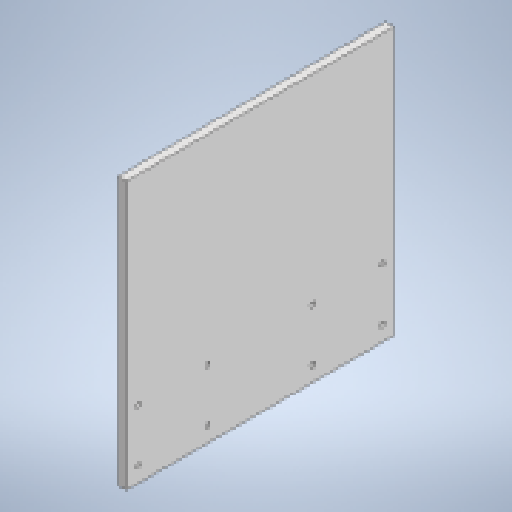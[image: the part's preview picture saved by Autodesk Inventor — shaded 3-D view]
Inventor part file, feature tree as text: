
AUTODESK INVENTOR PART (.ipt)
format: ipt  version: 2023 (Build 270158000, 158)  size: 148,480 bytes
history: native  units: in
note: dims shown in document units (in); Inventor stores cm internally (conversion verified against a paired STEP export)
features: extrude x2, sketch x2
ambient origin geometry x8: Origin, YZ Plane, XZ Plane, XY Plane, X Axis, Y Axis, Z Axis, Center Point
bodies: Solid1 (feature_tree)
feature tree (4):
  extrude  "Extrusion1"  Depth=8.0in
  extrude  "Extrusion2"  Depth=0.25in
  sketch  "Sketch1"  dims[d0=8.0in d1=8.0in]
  sketch  "Sketch2"  dims[d2=1.0in d3=0.0in d4=0.1575in d5=2.0866in d6=1.5748in d7=0.3504in d8=0.3504in d9=0.25in d10=0.0in d11=1.2402in]
